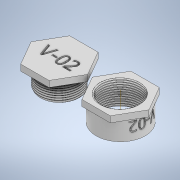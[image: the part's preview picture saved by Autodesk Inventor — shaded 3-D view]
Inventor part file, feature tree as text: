
AUTODESK INVENTOR PART (.ipt)
format: ipt  version: 2021.1 (Build 251245000, 245)  size: 924,160 bytes
history: native  units: in
note: dims shown in document units (in); Inventor stores cm internally (conversion verified against a paired STEP export)
features: sketch x9, extrude x6, helix x2, plane x1, emboss x1
ambient origin geometry x8: Origin, YZ Plane, XZ Plane, XY Plane, X Axis, Y Axis, Z Axis, Center Point
bodies: Body1 (feature_tree)
feature tree (19):
  extrude  "NutShaft"  Depth=1.0in
  helix  "CoilForNut"  [1 undecoded]
  extrude  "BoltHexHead"  Depth=0.0045in
  extrude  "BoltShaft"  Depth=0.0833in
  helix  "CoilForBolt"  [1 undecoded]
  extrude  "Extrusion5"  Depth=2.5in
  plane  "Work Plane4"
  emboss  "Emboss1"
  extrude  "Extrusion6"  Depth=0.25in
  extrude  "Extrusion7"  Depth=0.75in TaperAngle=0.0deg
  sketch  "Sketch4"  dims[d4=2.0in d5=1.5528in d6=1.0in d7=0.0in]
  sketch  "Sketch6"  dims[d33=60.0deg d35=0.0045in]
  sketch  "Sketch7"  dims[d36=0.8224in d37=0.0833in d38=0.0833in]
  sketch  "Sketch8"  dims[d39=1.2in d40=0.3937in d41=0.0in d42=90.0deg d43=90.0deg d44=0.0in d45=0.0in d46=2.5in]
  sketch  "Sketch9"  dims[d47=0.25in d48=0.0in d49=1.6118in]
  sketch  "Sketch11"  dims[d50=2.0in d51=0.75in d52=0.0in]
  sketch  "Sketch12"  dims[d53=60.0deg]
  sketch  "Sketch13"  dims[d54=0.0074in]
  sketch  "Sketch14"  dims[d56=0.8059in d57=0.7518in d58=0.0833in d59=1.0in d60=0.3937in d61=0.0in d62=90.0deg d63=90.0deg d64=0.0in d65=0.0in d66=0.0833in d68=0.1in d69=0.0in d70=1.0in d71=0.1in d72=0.0in d73=2.0in d74=0.25in d75=0.0in d76=0.75in d77=0.0in]
note: 2 required parameter values undecoded (feature->parameter linkage not recoverable at this tier; creation-order binding heuristic only, values carry confidence <= 0.55)
